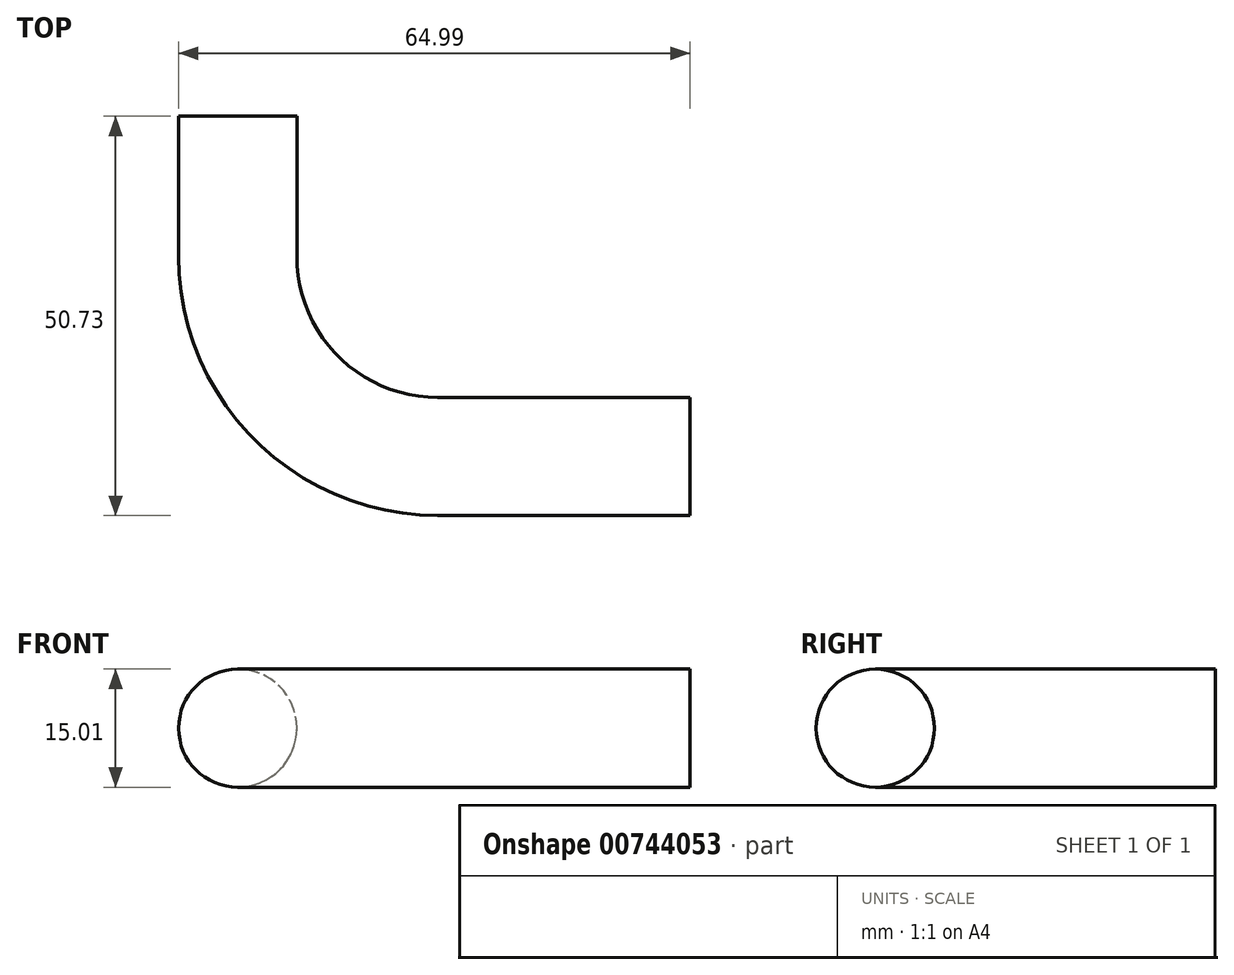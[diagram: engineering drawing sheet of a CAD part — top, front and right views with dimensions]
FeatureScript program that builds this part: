
annotation { "Feature Type Name" : "Feature", "Feature Type Description" : "" }
export const myFeature = defineFeature(function(context is Context, id is Id, definition is map)
    precondition{}
    {
        {
            var Q0;
            Q0=qCreatedBy(makeId("Right.planeOp"),FACE);
            var sketch = newSketch(context, id + "F0", { "sketchPlane" : qUnion([Q0])});
            skCircle(sketch, "E0", {"center": v(-48.64, 14.8) * mm, "radius": 7.5 * mm});
            skLineSegment(sketch, "E1", {"start": v(-48.64, 14.8) * mm, "end": v(-48.64, 40.82) * mm, "construction": true});
            skLineSegment(sketch, "E2", {"start": v(-48.64, 14.8) * mm, "end": v(-31.3, 14.8) * mm, "construction": true});
            skSolve(sketch);
        }
        {
            var Q0;
            Q0=qCreatedBy(makeId("Top.planeOp"),FACE);
            var Q1;
            Q1=sQuery(id+"F0.wireOp",VERTEX,"E1.start");
            cPlane(context, id + "F1", {"entities" : qUnion([Q0, Q1]), "cplaneType" : CPlaneType.PLANE_POINT, "offset" : 25.4 * mm, "width" : 152.4 * mm, "height" : 152.4 * mm});
        }
        {
            var Q0;
            Q0=qCreatedBy(id+"F1.planeOp",FACE);
            var sketch = newSketch(context, id + "F2", { "sketchPlane" : qUnion([Q0])});
            skLineSegment(sketch, "E3", {"start": v(0, -48.64) * mm, "end": v(-32.08, -48.64) * mm});
            skLineSegment(sketch, "E4", {"start": v(-57.48, -23.24) * mm, "end": v(-57.48, -5.41) * mm});
            skPoint(sketch, "E5.visualSharp", {"position": v(-57.48, -48.64) * mm});
            skArc(sketch, "E5.filletArc", {"start": v(-57.48, -23.24) * mm, "mid": v(-50.04, -41.2) * mm, "end": v(-32.08, -48.64) * mm});
            skSolve(sketch);
        }
        {
            var Q0;
            Q0 = qSketchRegion(id + "F0", true);
            var Q1;
            Q1 = qConstructionFilter(qBodyType(qCreatedBy(id + "F2" ,EDGE), BodyType.WIRE), ConstructionObject.NO);
            sweep(context, id + "F3", {"profiles" : qUnion([Q0]), "path" : qUnion([Q1])});
        }
    });
